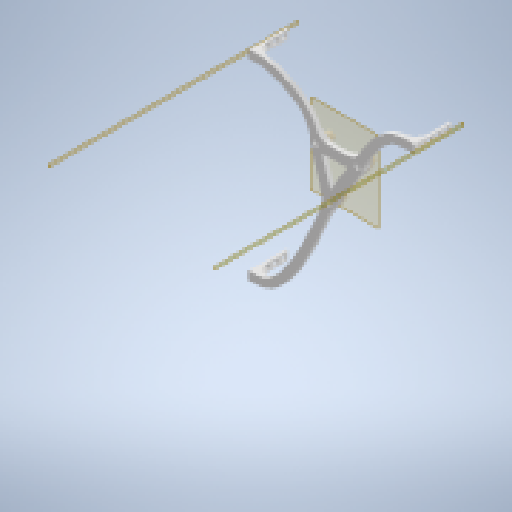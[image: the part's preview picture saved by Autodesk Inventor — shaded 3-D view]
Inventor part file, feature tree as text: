
AUTODESK INVENTOR PART (.ipt)
format: ipt  version: 2023 (Build 270158000, 158)  size: 525,824 bytes
history: native  units: mm
features: other x26, sketch x7, extrude x7, projected_geometry x5, fillet x3
ambient origin geometry x8: Origin, YZ Plane, XZ Plane, XY Plane, X Axis, Y Axis, Z Axis, Center Point
bodies: Solide1 (feature_tree)
feature tree (48):
  other  "Plan de construction1"
  sketch  "Esquisse1"
  other  "Plan de construction2"
  extrude  "Extrusion1"  Depth=2.5mm
  extrude  "Extrusion2"  Depth=2.5mm
  extrude  "Extrusion3"  Depth=2.5mm
  extrude  "Extrusion4"  Depth=10.0mm TaperAngle=0.0deg
  extrude  "Extrusion5"  Depth=5.0mm TaperAngle=0.0deg
  fillet  "Congé1"  Radius=12.0mm
  fillet  "Congé2"  Radius=12.0mm
  other  "Plan de construction3"
  other  "Plan de construction4"
  other  "Plan de construction5"
  extrude  "Extrusion8"  Depth=12.0mm
  other  "Plan de construction6"
  extrude  "Extrusion9"  Depth=5.0mm TaperAngle=0.0deg
  fillet  "Congé4"  Radius=5.8mm
  other  "Référence1"
  other  "Référence2"
  other  "Référence3"
  sketch  "Esquisse3"
  projected_geometry  "Boucle projetée1"
  projected_geometry  "Boucle projetée2"
  projected_geometry  "Boucle projetée3"
  sketch  "Esquisse4"
  projected_geometry  "Boucle projetée4"
  sketch  "Esquisse5"
  sketch  "Esquisse7"
  projected_geometry  "Boucle projetée6"
  other  "Référence4"
  other  "Référence5"
  other  "Référence6"
  sketch  "Esquisse10"
  other  "Référence9"
  other  "Référence10"
  sketch  "Esquisse11"
  other  "<userpath>\Desktop\export\iks01A2\iks01A2.iam"
  other  "iks01A2.iam"
  other  "NUCLEO-F411RE:1"
  other  "<userpath>\Desktop\export\Robotbebou.iam"
  other  "Robotbebou.iam"
  other  "MakerBeam-cube:1"
  other  "MakerBeam-cube_MIR1:1"
  other  "MakerBeam-cube_MIR_MIR:1"
  other  "MakerBeam-cube_MIR_MIR1_MIR:1"
  other  "MakerBeam-cube_MIR_MIR2:1"
  other  "profile259_MIR_MIR:1"
  other  "profile259_MIR:1"
